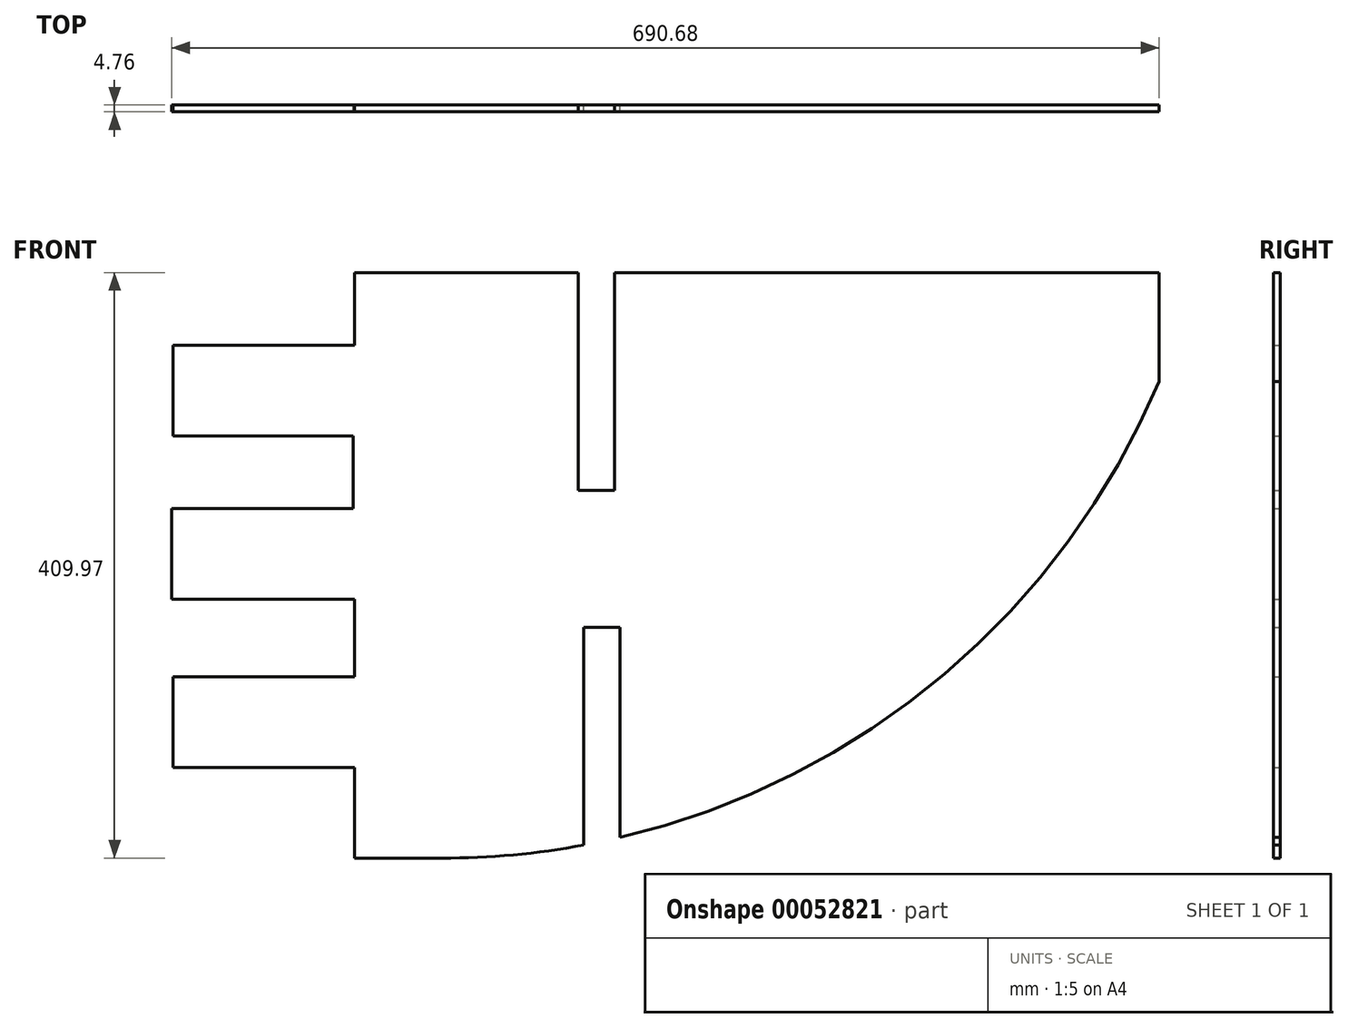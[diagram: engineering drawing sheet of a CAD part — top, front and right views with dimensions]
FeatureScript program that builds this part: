
annotation { "Feature Type Name" : "Feature", "Feature Type Description" : "" }
export const myFeature = defineFeature(function(context is Context, id is Id, definition is map)
    precondition{}
    {
        {
            var Q0;
            Q0=qCreatedBy(makeId("Front.planeOp"),FACE);
            var sketch = newSketch(context, id + "F0", { "sketchPlane" : qUnion([Q0])});
            skLineSegment(sketch, "E0", {"start": v(0, -409.97) * mm, "end": v(0, -346.47) * mm});
            skLineSegment(sketch, "E1", {"start": v(0, -50.8) * mm, "end": v(-127, -50.8) * mm});
            skLineSegment(sketch, "E2", {"start": v(-127, -50.8) * mm, "end": v(-127, -114.3) * mm});
            skLineSegment(sketch, "E3", {"start": v(-127, -114.3) * mm, "end": v(-1, -114.3) * mm});
            skLineSegment(sketch, "E4", {"start": v(-1, -165.1) * mm, "end": v(-128, -165.1) * mm});
            skLineSegment(sketch, "E5", {"start": v(-128, -165.1) * mm, "end": v(-128, -228.6) * mm});
            skLineSegment(sketch, "E6", {"start": v(-128, -228.6) * mm, "end": v(0, -228.6) * mm});
            skLineSegment(sketch, "E7", {"start": v(0, -282.97) * mm, "end": v(-127, -282.97) * mm});
            skLineSegment(sketch, "E8", {"start": v(-127, -282.97) * mm, "end": v(-127, -346.47) * mm});
            skLineSegment(sketch, "E9", {"start": v(-127, -346.47) * mm, "end": v(0, -346.47) * mm});
            skLineSegment(sketch, "E10.trimOffspring", {"start": v(0, -50.8) * mm, "end": v(0, 0) * mm});
            skLineSegment(sketch, "E11", {"start": v(0, 0) * mm, "end": v(156.27, 0) * mm});
            skLineSegment(sketch, "E12", {"start": v(562.67, 0) * mm, "end": v(562.67, -76.2) * mm});
            skLineSegment(sketch, "E13", {"start": v(0, -409.97) * mm, "end": v(60.96, -409.97) * mm});
            skArc(sketch, "E14", {"start": v(60.96, -409.97) * mm, "mid": v(110.83, -407.68) * mm, "end": v(160.28, -400.83) * mm});
            skPoint(sketch, "E15.start.orphan", {"position": v(-558.8, 0) * mm});
            skLineSegment(sketch, "E16", {"start": v(-1, -114.3) * mm, "end": v(-1, -165.1) * mm});
            skLineSegment(sketch, "E17", {"start": v(0, -228.6) * mm, "end": v(0, -282.97) * mm});
            skLineSegment(sketch, "E18", {"start": v(156.27, 0) * mm, "end": v(156.27, -152.4) * mm});
            skLineSegment(sketch, "E19", {"start": v(156.27, -152.4) * mm, "end": v(181.67, -152.4) * mm});
            skLineSegment(sketch, "E20", {"start": v(181.67, -152.4) * mm, "end": v(181.67, 0) * mm});
            skLineSegment(sketch, "E21.trimOffspring", {"start": v(181.67, 0) * mm, "end": v(562.67, 0) * mm});
            skLineSegment(sketch, "E22", {"start": v(160.28, -400.83) * mm, "end": v(160.28, -248.43) * mm});
            skLineSegment(sketch, "E23", {"start": v(160.28, -248.43) * mm, "end": v(185.68, -248.43) * mm});
            skLineSegment(sketch, "E24", {"start": v(185.68, -248.43) * mm, "end": v(185.68, -395.48) * mm});
            skArc(sketch, "E25.trimOffspring", {"start": v(185.68, -395.48) * mm, "mid": v(412.51, -281.1) * mm, "end": v(562.67, -76.2) * mm});
            skSolve(sketch);
        }
        {
            var Q0;
            Q0=makeQuery(id+"F0.imprint","IMPRINT",FACE,{"disambiguationData":[TD([[makeQuery(id+"F0.imprint","IMPRINT",EDGE,{"derivedFrom":sQuery(id+"F0.wireOp",EDGE,"E0")}),-1.0]])]});
            extrude(context, id + "F1", {"entities" : qUnion([Q0]), "depth" : 4.76 * mm});
        }
    });
